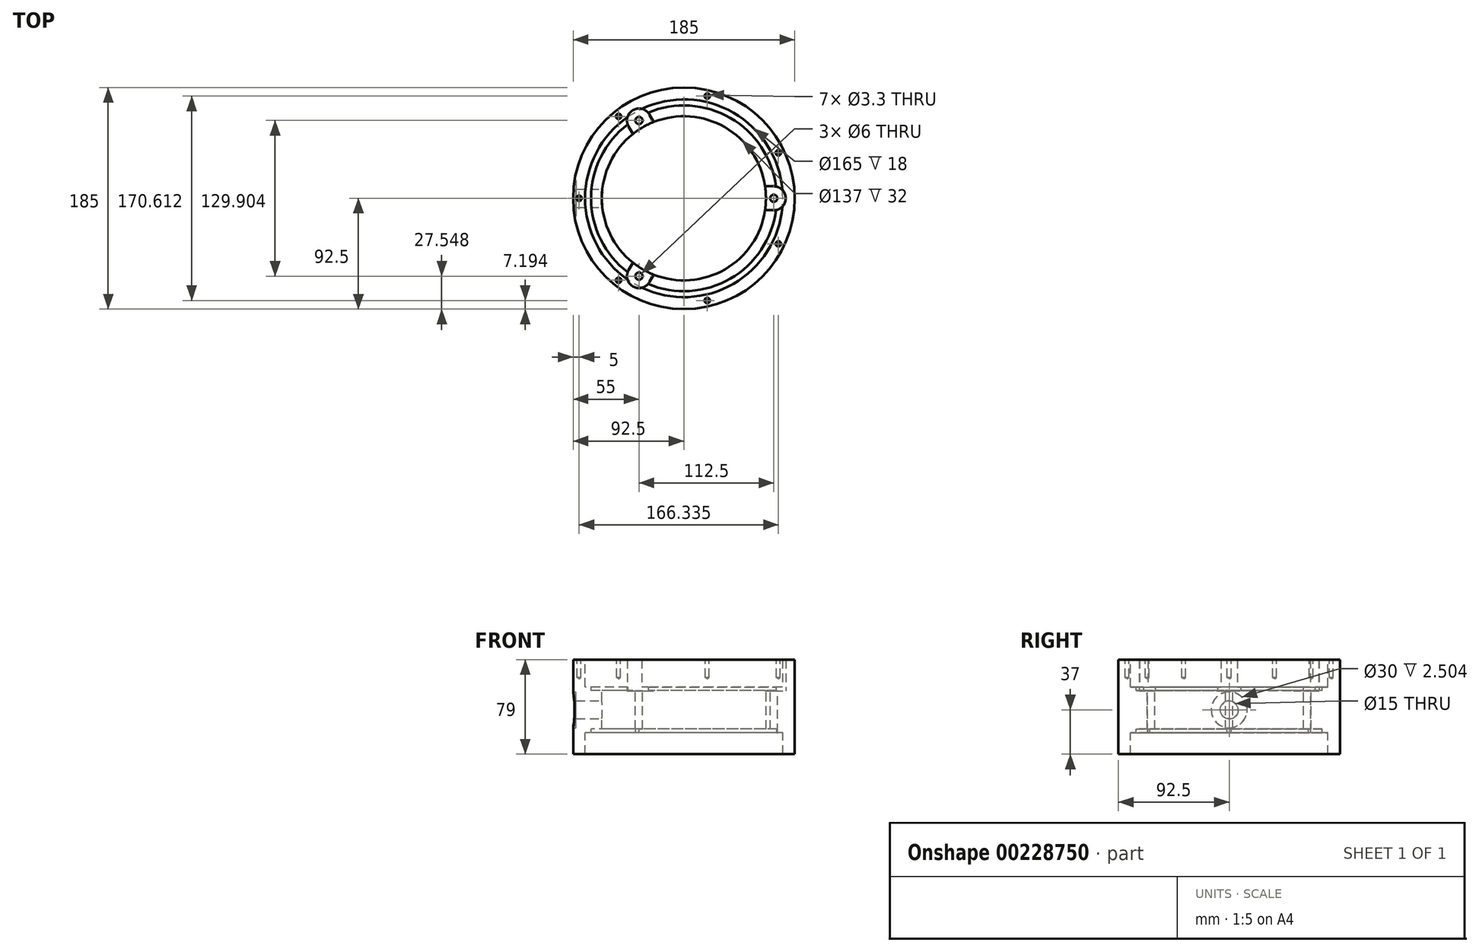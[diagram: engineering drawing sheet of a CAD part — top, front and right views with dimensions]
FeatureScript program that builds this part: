
annotation { "Feature Type Name" : "Feature", "Feature Type Description" : "" }
export const myFeature = defineFeature(function(context is Context, id is Id, definition is map)
    precondition{}
    {
        {
            var Q0;
            Q0=qCreatedBy(makeId("Front.planeOp"),FACE);
            var sketch = newSketch(context, id + "F0", { "sketchPlane" : qUnion([Q0])});
            skLineSegment(sketch, "E0", {"start": v(77.5, 18) * mm, "end": v(82.5, 18) * mm});
            skLineSegment(sketch, "E1", {"start": v(82.5, 18) * mm, "end": v(82.5, 0) * mm});
            skLineSegment(sketch, "E2", {"start": v(82.5, 0) * mm, "end": v(92.5, 0) * mm});
            skLineSegment(sketch, "E3", {"start": v(92.5, 0) * mm, "end": v(92.5, 79) * mm});
            skLineSegment(sketch, "E4", {"start": v(92.5, 79) * mm, "end": v(82.5, 79) * mm});
            skLineSegment(sketch, "E5", {"start": v(82.5, 79) * mm, "end": v(82.5, 56) * mm});
            skLineSegment(sketch, "E6", {"start": v(82.5, 56) * mm, "end": v(77.5, 56) * mm});
            skLineSegment(sketch, "E7", {"start": v(77.5, 56) * mm, "end": v(77.5, 53) * mm});
            skLineSegment(sketch, "E8", {"start": v(0, 73.69) * mm, "end": v(0, -17.93) * mm, "construction": true});
            skLineSegment(sketch, "E9", {"start": v(77.5, 53) * mm, "end": v(68.5, 53) * mm});
            skLineSegment(sketch, "E10", {"start": v(68.5, 53) * mm, "end": v(68.5, 21) * mm});
            skLineSegment(sketch, "E11", {"start": v(68.5, 21) * mm, "end": v(77.5, 21) * mm});
            skLineSegment(sketch, "E12.trimOffspring", {"start": v(77.5, 21) * mm, "end": v(77.5, 18) * mm});
            skSolve(sketch);
        }
        {
            var Q0;
            Q0 = qSketchRegion(id + "F0", true);
            var Q1;
            Q1=sQuery(id+"F0.wireOp",EDGE,"E8");
            revolve(context, id + "F1", {"entities" : qUnion([Q0]), "axis" : qUnion([Q1]), "revolveType" : RevolveType.FULL});
        }
        {
            var Q0;
            Q0=makeQuery(id+"F1.opRevolve","SWEPT_FACE",FACE,{"disambiguationData":[OSD([sQuery(id+"F0.wireOp",EDGE,"E9")])]});
            var sketch = newSketch(context, id + "F2", { "sketchPlane" : qUnion([Q0])});
            skCircle(sketch, "E13", {"center": v(0, 0) * mm, "radius": 75 * mm, "construction": true});
            skLineSegment(sketch, "E14", {"start": v(0, 0) * mm, "end": v(75, 0) * mm, "construction": true});
            skArc(sketch, "E15", {"start": v(74.33, -9.98) * mm, "mid": v(85, 0) * mm, "end": v(74.33, 9.98) * mm});
            skLineSegment(sketch, "E16", {"start": v(50, 10) * mm, "end": v(75, 10) * mm});
            skLineSegment(sketch, "E17", {"start": v(50, 10) * mm, "end": v(50, -10) * mm});
            skLineSegment(sketch, "E18", {"start": v(50, -10) * mm, "end": v(75, -10) * mm});
            skArc(sketch, "E19.1.0", {"start": v(-28.53, 69.36) * mm, "mid": v(-42.5, 73.61) * mm, "end": v(-45.8, 59.39) * mm});
            skLineSegment(sketch, "E19.1.1", {"start": v(-16.34, 48.3) * mm, "end": v(-28.84, 69.95) * mm});
            skLineSegment(sketch, "E19.1.2", {"start": v(-33.66, 38.3) * mm, "end": v(-16.34, 48.3) * mm});
            skLineSegment(sketch, "E19.1.3", {"start": v(-33.66, 38.3) * mm, "end": v(-46.16, 59.95) * mm});
            skArc(sketch, "E19.2.0", {"start": v(-45.8, -59.39) * mm, "mid": v(-42.5, -73.61) * mm, "end": v(-28.53, -69.36) * mm});
            skLineSegment(sketch, "E19.2.1", {"start": v(-33.66, -38.3) * mm, "end": v(-46.16, -59.95) * mm});
            skLineSegment(sketch, "E19.2.2", {"start": v(-16.34, -48.3) * mm, "end": v(-33.66, -38.3) * mm});
            skLineSegment(sketch, "E19.2.3", {"start": v(-16.34, -48.3) * mm, "end": v(-28.84, -69.95) * mm});
            skSolve(sketch);
        }
        {
            var Q0;
            Q0 = qSketchRegion(id + "F2", true);
            var Q1;
            Q1=makeQuery(id+"F1.opRevolve","SWEPT_FACE",FACE,{"disambiguationData":[OSD([sQuery(id+"F0.wireOp",EDGE,"E4")])]});
            extrude(context, id + "F3", {"entities" : qUnion([Q0]), "operationType" : NewBodyOperationType.REMOVE, "endBound" : BoundingType.UP_TO_SURFACE, "endBoundEntityFace" : qUnion([Q1]), "depth" : 25 * mm, "hasSecondDirection" : true, "secondDirectionOppositeDirection" : true, "secondDirectionDepth" : 0.2 * mm});
        }
        {
            var Q0;
            Q0=makeQuery(id+"F3.boolean.opBoolean","COPY",FACE,{"derivedFrom":makeQuery(id+"F3.opExtrude","CAP_FACE",FACE,{"disambiguationData":[OSD([sQuery(id+"F2.wireOp",EDGE,"E15"),sQuery(id+"F2.wireOp",EDGE,"E16"),sQuery(id+"F2.wireOp",EDGE,"E17"),sQuery(id+"F2.wireOp",EDGE,"E18")])],"isStart":true})});
            var sketch = newSketch(context, id + "F4", { "sketchPlane" : qUnion([Q0])});
            skPoint(sketch, "E20", {"position": v(75, 0) * mm});
            skPoint(sketch, "E21", {"position": v(-37.5, 64.95) * mm});
            skPoint(sketch, "E22", {"position": v(-37.5, -64.95) * mm});
            skSolve(sketch);
        }
        {
            var Q0;
            Q0=sQuery(id+"F4.wireOp",VERTEX,"E20");
            var Q1;
            Q1=sQuery(id+"F4.wireOp",VERTEX,"E21");
            var Q2;
            Q2=sQuery(id+"F4.wireOp",VERTEX,"E22");
            var Q3;
            Q3=makeQuery(id+"F1.opRevolve","SWEPT_BODY",BODY,{"disambiguationData":[OSD([sQuery(id+"F0.wireOp",EDGE,"E0"),sQuery(id+"F0.wireOp",EDGE,"E1"),sQuery(id+"F0.wireOp",EDGE,"E2"),sQuery(id+"F0.wireOp",EDGE,"E3"),sQuery(id+"F0.wireOp",EDGE,"E4"),sQuery(id+"F0.wireOp",EDGE,"E5"),sQuery(id+"F0.wireOp",EDGE,"E6"),sQuery(id+"F0.wireOp",EDGE,"E7"),sQuery(id+"F0.wireOp",EDGE,"E9"),sQuery(id+"F0.wireOp",EDGE,"E10"),sQuery(id+"F0.wireOp",EDGE,"E11"),sQuery(id+"F0.wireOp",EDGE,"E12.trimOffspring")])]});
            hole(context, id + "F5", {"style" : HoleStyle.SIMPLE, "endStyle" : HoleEndStyle.THROUGH, "holeDiameter" : 6 * mm, "locations" : qUnion([Q0, Q1, Q2]), "scope" : qUnion([Q3]), "isTappedThrough" : true});
        }
        {
            var Q0;
            Q0=qCreatedBy(makeId("Front.planeOp"),FACE);
            var sketch = newSketch(context, id + "F6", { "sketchPlane" : qUnion([Q0])});
            skLineSegment(sketch, "E23", {"start": v(-95, 37) * mm, "end": v(-65, 37) * mm});
            skLineSegment(sketch, "E24", {"start": v(-65, 37) * mm, "end": v(-65, 44.5) * mm});
            skLineSegment(sketch, "E25", {"start": v(-65, 44.5) * mm, "end": v(-90, 44.5) * mm});
            skLineSegment(sketch, "E26", {"start": v(-90, 44.5) * mm, "end": v(-90, 52) * mm});
            skLineSegment(sketch, "E27", {"start": v(-90, 52) * mm, "end": v(-95, 52) * mm});
            skLineSegment(sketch, "E28", {"start": v(-95, 52) * mm, "end": v(-95, 37) * mm});
            skSolve(sketch);
        }
        {
            var Q0;
            Q0 = qSketchRegion(id + "F6", true);
            var Q1;
            Q1=sQuery(id+"F6.wireOp",EDGE,"E23");
            revolve(context, id + "F7", {"operationType" : NewBodyOperationType.REMOVE, "entities" : qUnion([Q0]), "axis" : qUnion([Q1]), "revolveType" : RevolveType.FULL, "oppositeDirection" : true});
        }
        {
            var Q0;
            Q0=makeQuery(id+"F1.opRevolve","SWEPT_FACE",FACE,{"disambiguationData":[OSD([sQuery(id+"F0.wireOp",EDGE,"E4")])]});
            var sketch = newSketch(context, id + "F8", { "sketchPlane" : qUnion([Q0])});
            skCircle(sketch, "E29", {"center": v(0, 0) * mm, "radius": 87.5 * mm, "construction": true});
            skLineSegment(sketch, "E30", {"start": v(0, 0) * mm, "end": v(-87.5, 0) * mm, "construction": true});
            skPoint(sketch, "E31", {"position": v(-87.5, 0) * mm});
            skPoint(sketch, "E32.1.0", {"position": v(-54.56, -68.41) * mm});
            skPoint(sketch, "E32.2.0", {"position": v(19.47, -85.3) * mm});
            skPoint(sketch, "E32.3.0", {"position": v(78.83, -37.96) * mm});
            skPoint(sketch, "E32.4.0", {"position": v(78.83, 37.96) * mm});
            skPoint(sketch, "E32.5.0", {"position": v(19.47, 85.3) * mm});
            skPoint(sketch, "E32.6.0", {"position": v(-54.56, 68.41) * mm});
            skSolve(sketch);
        }
        {
            var Q0;
            Q0=sQuery(id+"F8.wireOp",VERTEX,"E31");
            var Q1;
            Q1=sQuery(id+"F8.wireOp",VERTEX,"E32.6.0");
            var Q2;
            Q2=sQuery(id+"F8.wireOp",VERTEX,"E32.5.0");
            var Q3;
            Q3=sQuery(id+"F8.wireOp",VERTEX,"E32.4.0");
            var Q4;
            Q4=sQuery(id+"F8.wireOp",VERTEX,"E32.3.0");
            var Q5;
            Q5=sQuery(id+"F8.wireOp",VERTEX,"E32.2.0");
            var Q6;
            Q6=sQuery(id+"F8.wireOp",VERTEX,"E32.1.0");
            var Q7;
            Q7=makeQuery(id+"F1.opRevolve","SWEPT_BODY",BODY,{"disambiguationData":[OSD([sQuery(id+"F0.wireOp",EDGE,"E0"),sQuery(id+"F0.wireOp",EDGE,"E1"),sQuery(id+"F0.wireOp",EDGE,"E2"),sQuery(id+"F0.wireOp",EDGE,"E3"),sQuery(id+"F0.wireOp",EDGE,"E4"),sQuery(id+"F0.wireOp",EDGE,"E5"),sQuery(id+"F0.wireOp",EDGE,"E6"),sQuery(id+"F0.wireOp",EDGE,"E7"),sQuery(id+"F0.wireOp",EDGE,"E9"),sQuery(id+"F0.wireOp",EDGE,"E10"),sQuery(id+"F0.wireOp",EDGE,"E11"),sQuery(id+"F0.wireOp",EDGE,"E12.trimOffspring")])]});
            hole(context, id + "F9", {"style" : HoleStyle.C_SINK, "endStyle" : HoleEndStyle.BLIND, "holeDiameter" : 3.3 * mm, "cSinkDiameter" : 4.5 * mm, "cSinkAngle" : 90 * degree, "holeDepth" : 15 * mm, "locations" : qUnion([Q0, Q1, Q2, Q3, Q4, Q5, Q6]), "scope" : qUnion([Q7])});
        }
    });
